# Revit family: CL 40 (a)
name_source: partatom
category: Equipement spécialisé
revit_build: Autodesk Revit LT 2015 (Build: 20140606_1530(x64)
units: mm (PartAtom-declared; Revit-internal decimal feet)

## types (5) — shared parameters
Apparent Power = 0 VA
Description = COUPE-LEGUMES
Electrique connexion = 40 mm  [stored 0.131234 ft]
Fabricant = ROBOT COUPE
Height = 590 mm
Phase = 1
UP Height = 685 mm
UP Width = 421 mm
URL = www.robot-coupe.com
Width = 358 mm
water = Connector
zero-valued in all types: Cold water supply, Cold water supply height, Top, Used water, Waste water height

## per-type parameters (varying)
| type | Amps | Cycle | Depth | HP | Modèle | Speeds (Rpm) | Volts | Watts | Weight |
| CL 40   230/50/1 | 5.4 A | 50 Hz | 304 mm |  | CL 40 | 500 | 230 V | 500 W | 15.2 kg |
| CL 40   120/60/1 | 12 A | 60 Hz | 325 mm  [stored 1.06627 ft] |  | CL 40 | 500 | 120 V | 500 W | 15.2 kg |
| CL 40   220/60/1 | 5.4 A | 60 Hz | 304 mm |  | CL 40 | 500 | 220 V | 500 W | 15.2 kg |
| CL 40   220-240/50/1 | 5.4 A | 50 Hz | 304 mm |  | CL 40 | 500 | 220 V | 500 W | 15.2 kg |
| CL 40 USA   120/60/1 | 12 A | 60 Hz | 325 mm  [stored 1.06627 ft] | 1 | CL 40 USA | 600 | 120 V | 0 W | 40 lbs |

note: [stored X ft] marks values corroborated as IEEE doubles in the binary element streams (Revit-internal decimal feet)

## geometry (parser evidence)
native form markers: Blend x104, Sweep x4
no freeform markers — native parametric forms only
